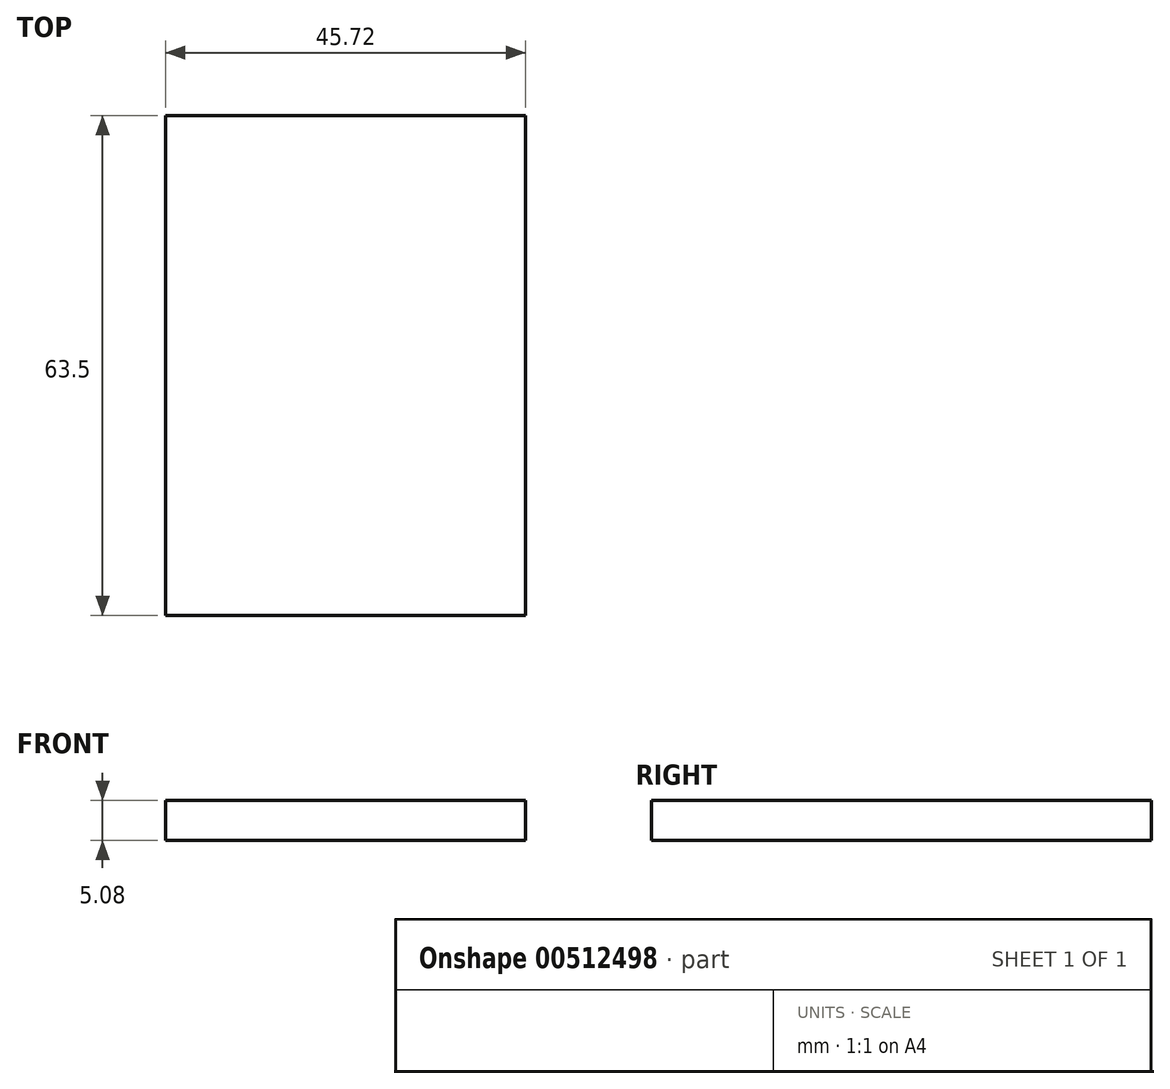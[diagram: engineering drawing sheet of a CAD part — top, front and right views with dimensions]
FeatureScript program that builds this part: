
annotation { "Feature Type Name" : "Feature", "Feature Type Description" : "" }
export const myFeature = defineFeature(function(context is Context, id is Id, definition is map)
    precondition{}
    {
        {
            var Q0;
            Q0=qCreatedBy(makeId("Top.planeOp"),FACE);
            var sketch = newSketch(context, id + "F0", { "sketchPlane" : qUnion([Q0])});
            skLineSegment(sketch, "E0.bottom", {"start": v(-37.06, -28.6) * mm, "end": v(8.66, -28.6) * mm});
            skLineSegment(sketch, "E0.top", {"start": v(-37.06, 34.9) * mm, "end": v(8.66, 34.9) * mm});
            skLineSegment(sketch, "E0.left", {"start": v(-37.06, -28.6) * mm, "end": v(-37.06, 34.9) * mm});
            skLineSegment(sketch, "E0.right", {"start": v(8.66, -28.6) * mm, "end": v(8.66, 34.9) * mm});
            skSolve(sketch);
        }
        {
            var Q0;
            Q0=makeQuery(id+"F0.imprint","IMPRINT",FACE,{"disambiguationData":[TD([[makeQuery(id+"F0.imprint","IMPRINT",EDGE,{"derivedFrom":sQuery(id+"F0.wireOp",EDGE,"E0.bottom")}),1.0]])]});
            extrude(context, id + "F1", {"entities" : qUnion([Q0]), "depth" : 5.08 * mm});
        }
    });
